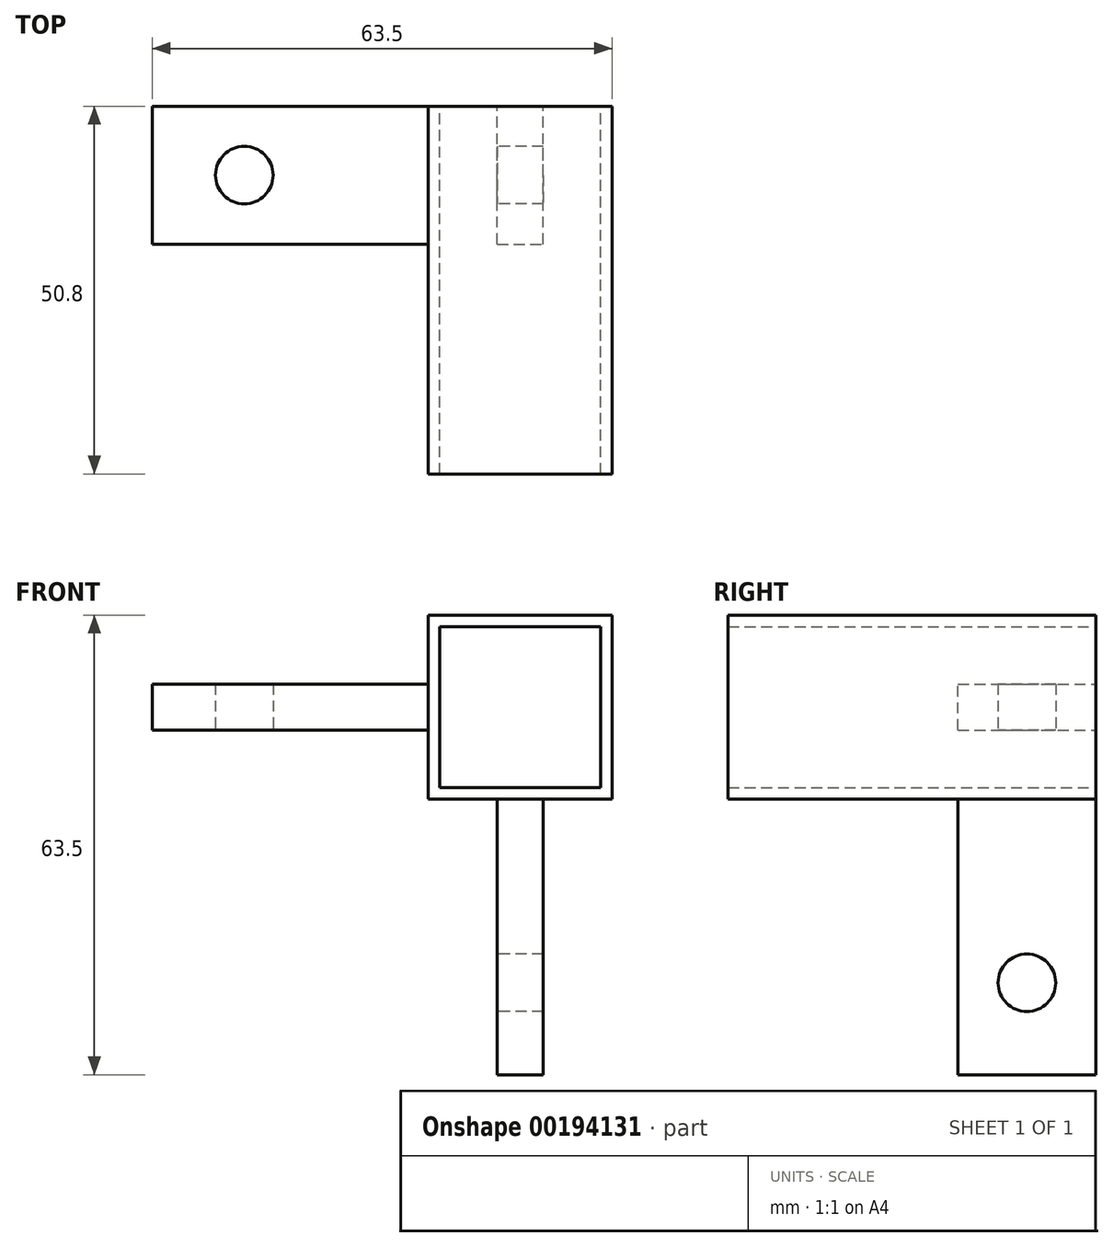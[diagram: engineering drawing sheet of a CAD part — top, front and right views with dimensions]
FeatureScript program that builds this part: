
annotation { "Feature Type Name" : "Feature", "Feature Type Description" : "" }
export const myFeature = defineFeature(function(context is Context, id is Id, definition is map)
    precondition{}
    {
        {
            var Q0;
            Q0=qCreatedBy(makeId("Front.planeOp"),FACE);
            var sketch = newSketch(context, id + "F0", { "sketchPlane" : qUnion([Q0])});
            skLineSegment(sketch, "E0.bottom", {"start": v(0, 0) * mm, "end": v(25.4, 0) * mm});
            skLineSegment(sketch, "E0.top", {"start": v(0, 25.4) * mm, "end": v(25.4, 25.4) * mm});
            skLineSegment(sketch, "E0.left", {"start": v(0, 0) * mm, "end": v(0, 25.4) * mm});
            skLineSegment(sketch, "E0.right", {"start": v(25.4, 0) * mm, "end": v(25.4, 25.4) * mm});
            skLineSegment(sketch, "E1.0", {"start": v(1.59, 1.59) * mm, "end": v(1.59, 23.81) * mm});
            skLineSegment(sketch, "E1.1", {"start": v(1.59, 1.59) * mm, "end": v(23.81, 1.59) * mm});
            skLineSegment(sketch, "E1.2", {"start": v(23.81, 1.59) * mm, "end": v(23.81, 23.81) * mm});
            skLineSegment(sketch, "E1.3", {"start": v(1.59, 23.81) * mm, "end": v(23.81, 23.81) * mm});
            skSolve(sketch);
        }
        {
            var Q0;
            Q0 = qSketchRegion(id + "F0", true);
            extrude(context, id + "F1", {"entities" : qUnion([Q0]), "depth" : 50.8 * mm});
        }
        {
            var Q0;
            Q0=qCreatedBy(makeId("Front.planeOp"),FACE);
            var sketch = newSketch(context, id + "F2", { "sketchPlane" : qUnion([Q0])});
            skLineSegment(sketch, "E2.bottom", {"start": v(9.53, 0) * mm, "end": v(15.88, 0) * mm});
            skLineSegment(sketch, "E2.top", {"start": v(9.53, -38.1) * mm, "end": v(15.88, -38.1) * mm});
            skLineSegment(sketch, "E2.left", {"start": v(9.53, 0) * mm, "end": v(9.53, -38.1) * mm});
            skLineSegment(sketch, "E2.right", {"start": v(15.88, 0) * mm, "end": v(15.88, -38.1) * mm});
            skLineSegment(sketch, "E3.bottom", {"start": v(0, 9.53) * mm, "end": v(-38.1, 9.53) * mm});
            skLineSegment(sketch, "E3.top", {"start": v(0, 15.88) * mm, "end": v(-38.1, 15.87) * mm});
            skLineSegment(sketch, "E3.left", {"start": v(0, 9.53) * mm, "end": v(0, 15.88) * mm});
            skLineSegment(sketch, "E3.right", {"start": v(-38.1, 9.52) * mm, "end": v(-38.1, 15.87) * mm});
            skSolve(sketch);
        }
        {
            var Q0;
            Q0 = qSketchRegion(id + "F2", true);
            extrude(context, id + "F3", {"entities" : qUnion([Q0]), "operationType" : NewBodyOperationType.ADD, "depth" : 19.05 * mm});
        }
        {
            var Q0;
            Q0=makeQuery(id+"F3.opExtrude","SWEPT_FACE",FACE,{"disambiguationData":[OSD([sQuery(id+"F2.wireOp",EDGE,"E2.left")])]});
            var sketch = newSketch(context, id + "F4", { "sketchPlane" : qUnion([Q0])});
            skCircle(sketch, "E4", {"center": v(9.53, -25.4) * mm, "radius": 3.98 * mm});
            skPoint(sketch, "E4.centerSnap0", {"position": v(9.53, -38.1) * mm});
            skSolve(sketch);
        }
        {
            var Q0;
            Q0 = qSketchRegion(id + "F4", true);
            extrude(context, id + "F5", {"entities" : qUnion([Q0]), "operationType" : NewBodyOperationType.REMOVE, "oppositeDirection" : true, "depth" : 25.4 * mm});
        }
        {
            var Q0;
            Q0=makeQuery(id+"F3.opExtrude","SWEPT_FACE",FACE,{"disambiguationData":[OSD([sQuery(id+"F2.wireOp",EDGE,"E3.bottom")])]});
            var sketch = newSketch(context, id + "F6", { "sketchPlane" : qUnion([Q0])});
            skCircle(sketch, "E5", {"center": v(-25.4, 9.53) * mm, "radius": 3.98 * mm});
            skPoint(sketch, "E5.centerSnap0", {"position": v(0, 9.53) * mm});
            skSolve(sketch);
        }
        {
            var Q0;
            Q0 = qSketchRegion(id + "F6", true);
            extrude(context, id + "F7", {"entities" : qUnion([Q0]), "operationType" : NewBodyOperationType.REMOVE, "oppositeDirection" : true, "depth" : 25.4 * mm});
        }
    });
